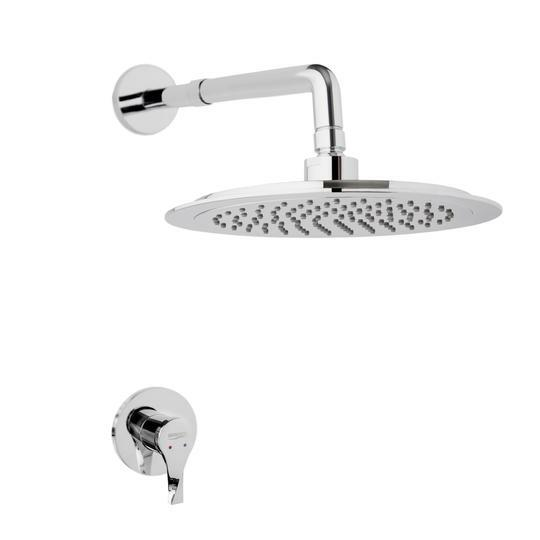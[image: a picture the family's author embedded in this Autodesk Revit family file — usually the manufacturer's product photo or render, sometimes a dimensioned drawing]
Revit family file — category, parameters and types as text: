
# Revit family: 01-2601-211 DUCHA MONOMANDO SIN SALIDA SION
name_source: partatom
category: Plumbing Fixtures
revit_build: Autodesk Revit 2018 (Build: 20170223_1515(x64)
units: mm (PartAtom-declared; Revit-internal decimal feet)

## family parameters
Cut with Voids When Loaded = No
Host = Face
OmniClass Number = 23.31.11.00
Part Type = Normal
Room Calculation Point = No
Round Connector Dimension = Use Diameter
Shared = No

## types (1)
- 01-2601-211
    Alto ducha a eje = 350 mm  [stored 1.14829 ft]
    Alto manija = 72 mm  [stored 0.23622 ft]
    CW Connection = Yes
    Default Elevation = 0 mm  [stored 0 ft]
    Description = Monomando ducha
    Dim ducha sion = 230 mm  [stored 0.754593 ft]
    Dim escudo manija = 120 mm
    HW Connection = Yes
    Largo manija = 110 mm
    Link Ficha Tecnica = http://infotecnica.gricol.com
    Manufacturer = Gricol
    Model = 01-2601-211
    Plastico ABS Cromado = Plastico - ABS Cromado
    Product Name = DUCHA MONOMANDO SIN SALIDA SION
    Type Image = DUCHA MONOMANDO SIN SALIDA SION.jpg
    URL = https://www.gricol.com
    Vent Connection = No
    Waste Connection = No

note: [stored X ft] marks values corroborated as IEEE doubles in the binary element streams (Revit-internal decimal feet)

## geometry (parser evidence)
native form markers: Blend x2, Sweep x18
no freeform markers — native parametric forms only
